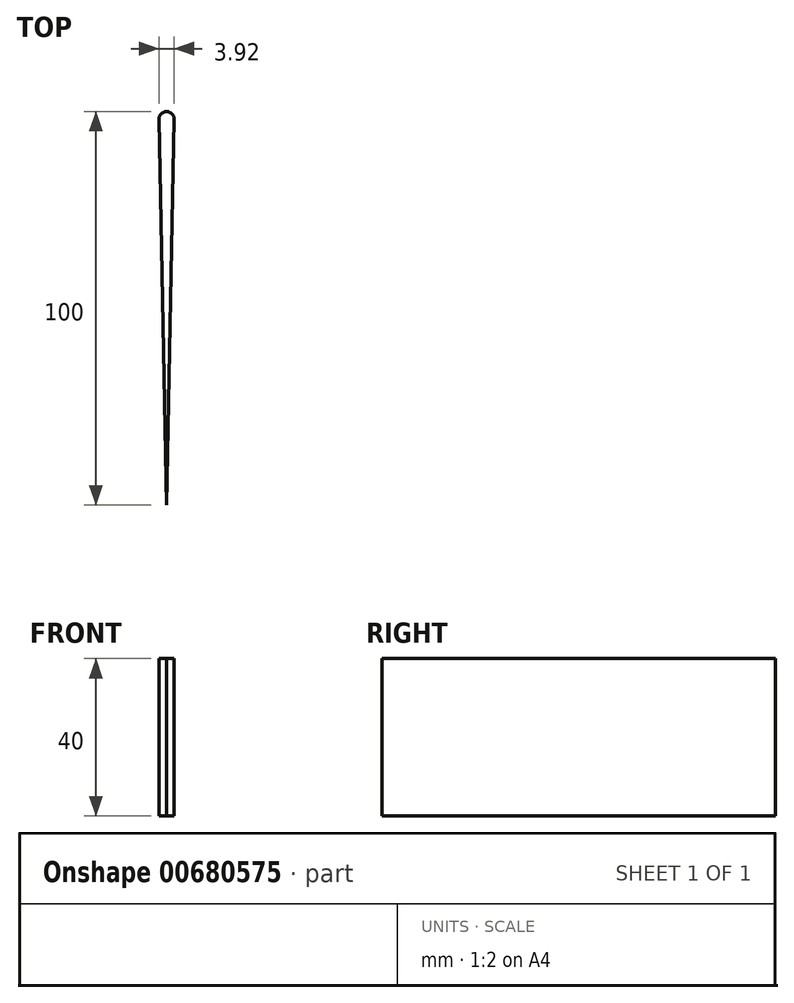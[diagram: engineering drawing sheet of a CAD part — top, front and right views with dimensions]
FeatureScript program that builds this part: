
annotation { "Feature Type Name" : "Feature", "Feature Type Description" : "" }
export const myFeature = defineFeature(function(context is Context, id is Id, definition is map)
    precondition{}
    {
        {
            var Q0;
            Q0=qCreatedBy(makeId("Top.planeOp"),FACE);
            var sketch = newSketch(context, id + "F0", { "sketchPlane" : qUnion([Q0])});
            skLineSegment(sketch, "E0", {"start": v(0, 0) * mm, "end": v(2, 0) * mm});
            skLineSegment(sketch, "E1", {"start": v(2, 0) * mm, "end": v(0, -100) * mm});
            skLineSegment(sketch, "E2", {"start": v(0, -100) * mm, "end": v(-2, 0) * mm});
            skLineSegment(sketch, "E3", {"start": v(-2, 0) * mm, "end": v(0, 0) * mm});
            skSolve(sketch);
        }
        {
            var Q0;
            Q0 = qSketchRegion(id + "F0", true);
            extrude(context, id + "F1", {"entities" : qUnion([Q0]), "depth" : 40 * mm, "offsetDistance" : 25 * mm});
        }
        {
            var Q0;
            Q0=makeQuery(id+"F1.opExtrude","SWEPT_EDGE",EDGE,{"disambiguationData":[OSD([sQuery(id+"F0.wireOp",EDGE,"E2"),sQuery(id+"F0.wireOp",EDGE,"E3")])]});
            var Q1;
            Q1=makeQuery(id+"F1.opExtrude","SWEPT_EDGE",EDGE,{"disambiguationData":[OSD([sQuery(id+"F0.wireOp",EDGE,"E0"),sQuery(id+"F0.wireOp",EDGE,"E1")])]});
            fillet(context, id + "F2", {"entities" : qUnion([Q0, Q1]), "radius" : 2 * mm, "tangentPropagation" : true, "allowEdgeOverflow" : false});
        }
    });
